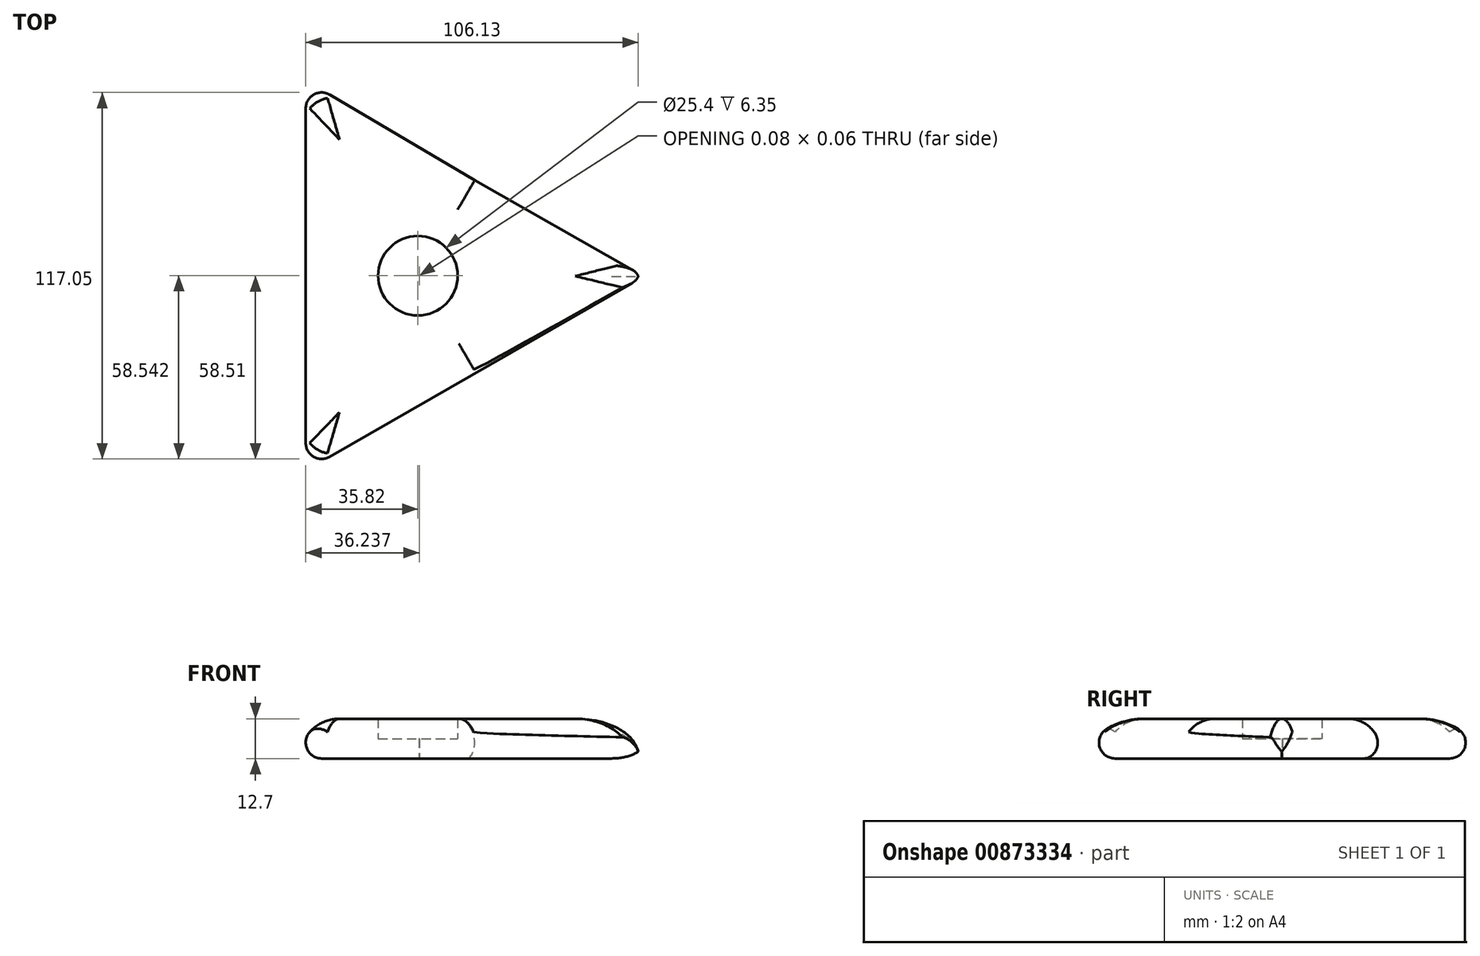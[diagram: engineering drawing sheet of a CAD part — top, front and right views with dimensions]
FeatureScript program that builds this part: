
annotation { "Feature Type Name" : "Feature", "Feature Type Description" : "" }
export const myFeature = defineFeature(function(context is Context, id is Id, definition is map)
    precondition{}
    {
        {
            var Q0;
            Q0=qCreatedBy(makeId("Top.planeOp"),FACE);
            var sketch = newSketch(context, id + "F0", { "sketchPlane" : qUnion([Q0])});
            skCircle(sketch, "E0", {"center": v(0, 0) * mm, "radius": 12.7 * mm});
            skSolve(sketch);
        }
        {
            var Q0;
            Q0=qCreatedBy(makeId("Top.planeOp"),FACE);
            var sketch = newSketch(context, id + "F1", { "sketchPlane" : qUnion([Q0])});
            skLineSegment(sketch, "E1", {"start": v(-37.76, 65.76) * mm, "end": v(19.45, -32.69) * mm});
            skLineSegment(sketch, "E2", {"start": v(19.45, -32.69) * mm, "end": v(75.7, 0) * mm});
            skLineSegment(sketch, "E3", {"start": v(75.7, 0) * mm, "end": v(-37.76, 0) * mm});
            skLineSegment(sketch, "E4", {"start": v(-37.76, 0) * mm, "end": v(-37.76, -65.56) * mm});
            skLineSegment(sketch, "E5", {"start": v(-37.76, -65.56) * mm, "end": v(19.09, 32.16) * mm});
            skLineSegment(sketch, "E6", {"start": v(19.09, 32.16) * mm, "end": v(-37.76, 65.76) * mm});
            skLineSegment(sketch, "E7", {"start": v(-37.76, 65.76) * mm, "end": v(-37.76, 0) * mm});
            skLineSegment(sketch, "E8", {"start": v(-37.76, 0) * mm, "end": v(75.7, 0) * mm});
            skLineSegment(sketch, "E9", {"start": v(19.09, 32.16) * mm, "end": v(75.7, 0) * mm});
            skLineSegment(sketch, "E10", {"start": v(-37.76, -65.56) * mm, "end": v(19.45, -32.69) * mm});
            skSolve(sketch);
        }
        {
            var Q0;
            Q0 = qSketchRegion(id + "F1", true);
            extrude(context, id + "F2", {"entities" : qUnion([Q0]), "endBound" : BoundingType.SYMMETRIC, "depth" : 12.7 * mm, "offsetDistance" : 25.4 * mm});
        }
        {
            var Q0;
            Q0=makeQuery(id+"F2.opExtrude","CAP_EDGE",EDGE,{"disambiguationData":[OSD([sQuery(id+"F1.wireOp",EDGE,"E4"),sQuery(id+"F1.wireOp",EDGE,"E7")])],"isStart":false});
            var Q1;
            Q1=makeQuery(id+"F2.opExtrude","CAP_EDGE",EDGE,{"disambiguationData":[OSD([sQuery(id+"F1.wireOp",EDGE,"E9")])],"isStart":false});
            var Q2;
            Q2=makeQuery(id+"F2.opExtrude","CAP_EDGE",EDGE,{"disambiguationData":[OSD([sQuery(id+"F1.wireOp",EDGE,"E6")])],"isStart":false});
            var Q3;
            Q3=makeQuery(id+"F2.opExtrude","CAP_EDGE",EDGE,{"disambiguationData":[OSD([sQuery(id+"F1.wireOp",EDGE,"E10")])],"isStart":false});
            fillet(context, id + "F3", {"entities" : qUnion([Q0, Q1, Q2, Q3]), "radius" : 12.7 * mm, "tangentPropagation" : true, "allowEdgeOverflow" : false});
        }
        {
            var Q0;
            {var subQ0=sQuery(id+"F1.wireOp",EDGE,"E7");var subQ1=sQuery(id+"F1.wireOp",EDGE,"E4");Q0=makeQuery(id+"F3.opFillet","BLEND_EDGE",EDGE,{"blendedFrom":[makeQuery(id+"F2.opExtrude","CAP_EDGE",EDGE,{"disambiguationData":[OSD([subQ1,subQ0])],"isStart":false}),makeQuery(id+"F2.opExtrude","CAP_FACE",FACE,{"disambiguationData":[OSD([sQuery(id+"F1.wireOp",EDGE,"E1"),sQuery(id+"F1.wireOp",EDGE,"E2"),subQ1,sQuery(id+"F1.wireOp",EDGE,"E5"),sQuery(id+"F1.wireOp",EDGE,"E6"),subQ0,sQuery(id+"F1.wireOp",EDGE,"E8"),sQuery(id+"F1.wireOp",EDGE,"E9"),sQuery(id+"F1.wireOp",EDGE,"E10")])],"isStart":true})],"blendedInto":[makeQuery(id+"F2.opExtrude","CAP_FACE",FACE,{"disambiguationData":[OSD([sQuery(id+"F1.wireOp",EDGE,"E1"),sQuery(id+"F1.wireOp",EDGE,"E2"),subQ1,sQuery(id+"F1.wireOp",EDGE,"E5"),sQuery(id+"F1.wireOp",EDGE,"E6"),subQ0,sQuery(id+"F1.wireOp",EDGE,"E8"),sQuery(id+"F1.wireOp",EDGE,"E9"),sQuery(id+"F1.wireOp",EDGE,"E10")])],"isStart":true})]});}
            var Q1;
            {var subQ0=sQuery(id+"F1.wireOp",EDGE,"E10");Q1=makeQuery(id+"F3.opFillet","BLEND_EDGE",EDGE,{"disambiguationData":[OD(0.0)],"blendedFrom":[makeQuery(id+"F2.opExtrude","CAP_EDGE",EDGE,{"disambiguationData":[OSD([subQ0])],"isStart":false}),makeQuery(id+"F2.opExtrude","CAP_FACE",FACE,{"disambiguationData":[OSD([sQuery(id+"F1.wireOp",EDGE,"E1"),sQuery(id+"F1.wireOp",EDGE,"E2"),sQuery(id+"F1.wireOp",EDGE,"E4"),sQuery(id+"F1.wireOp",EDGE,"E5"),sQuery(id+"F1.wireOp",EDGE,"E6"),sQuery(id+"F1.wireOp",EDGE,"E7"),sQuery(id+"F1.wireOp",EDGE,"E8"),sQuery(id+"F1.wireOp",EDGE,"E9"),subQ0])],"isStart":true})],"blendedInto":[makeQuery(id+"F2.opExtrude","CAP_FACE",FACE,{"disambiguationData":[OSD([sQuery(id+"F1.wireOp",EDGE,"E1"),sQuery(id+"F1.wireOp",EDGE,"E2"),sQuery(id+"F1.wireOp",EDGE,"E4"),sQuery(id+"F1.wireOp",EDGE,"E5"),sQuery(id+"F1.wireOp",EDGE,"E6"),sQuery(id+"F1.wireOp",EDGE,"E7"),sQuery(id+"F1.wireOp",EDGE,"E8"),sQuery(id+"F1.wireOp",EDGE,"E9"),subQ0])],"isStart":true})]});}
            var Q2;
            {var subQ0=sQuery(id+"F1.wireOp",EDGE,"E9");Q2=makeQuery(id+"F3.opFillet","BLEND_EDGE",EDGE,{"blendedFrom":[makeQuery(id+"F2.opExtrude","CAP_EDGE",EDGE,{"disambiguationData":[OSD([subQ0])],"isStart":false}),makeQuery(id+"F2.opExtrude","CAP_FACE",FACE,{"disambiguationData":[OSD([sQuery(id+"F1.wireOp",EDGE,"E1"),sQuery(id+"F1.wireOp",EDGE,"E2"),sQuery(id+"F1.wireOp",EDGE,"E4"),sQuery(id+"F1.wireOp",EDGE,"E5"),sQuery(id+"F1.wireOp",EDGE,"E6"),sQuery(id+"F1.wireOp",EDGE,"E7"),sQuery(id+"F1.wireOp",EDGE,"E8"),subQ0,sQuery(id+"F1.wireOp",EDGE,"E10")])],"isStart":true})],"blendedInto":[makeQuery(id+"F2.opExtrude","CAP_FACE",FACE,{"disambiguationData":[OSD([sQuery(id+"F1.wireOp",EDGE,"E1"),sQuery(id+"F1.wireOp",EDGE,"E2"),sQuery(id+"F1.wireOp",EDGE,"E4"),sQuery(id+"F1.wireOp",EDGE,"E5"),sQuery(id+"F1.wireOp",EDGE,"E6"),sQuery(id+"F1.wireOp",EDGE,"E7"),sQuery(id+"F1.wireOp",EDGE,"E8"),subQ0,sQuery(id+"F1.wireOp",EDGE,"E10")])],"isStart":true})]});}
            var Q3;
            Q3=makeQuery(id+"F3.opFillet","BLEND_EDGE",EDGE,{"blendedFrom":[makeQuery(id+"F2.opExtrude","CAP_EDGE",EDGE,{"disambiguationData":[OSD([sQuery(id+"F1.wireOp",EDGE,"E9")])],"isStart":false}),makeQuery(id+"F2.opExtrude","CAP_EDGE",EDGE,{"disambiguationData":[OSD([sQuery(id+"F1.wireOp",EDGE,"E10")])],"isStart":false})],"blendedInto":[]});
            var Q4;
            Q4=makeQuery(id+"F3.opFillet","BLEND_EDGE",EDGE,{"blendedFrom":[makeQuery(id+"F2.opExtrude","CAP_EDGE",EDGE,{"disambiguationData":[OSD([sQuery(id+"F1.wireOp",EDGE,"E4"),sQuery(id+"F1.wireOp",EDGE,"E7")])],"isStart":false}),makeQuery(id+"F2.opExtrude","CAP_EDGE",EDGE,{"disambiguationData":[OSD([sQuery(id+"F1.wireOp",EDGE,"E6")])],"isStart":false})],"blendedInto":[]});
            var Q5;
            Q5=makeQuery(id+"F3.opFillet","BLEND_EDGE",EDGE,{"blendedFrom":[makeQuery(id+"F2.opExtrude","CAP_EDGE",EDGE,{"disambiguationData":[OSD([sQuery(id+"F1.wireOp",EDGE,"E4"),sQuery(id+"F1.wireOp",EDGE,"E7")])],"isStart":false}),makeQuery(id+"F2.opExtrude","CAP_EDGE",EDGE,{"disambiguationData":[OSD([sQuery(id+"F1.wireOp",EDGE,"E10")])],"isStart":false})],"blendedInto":[]});
            fillet(context, id + "F4", {"entities" : qUnion([Q0, Q1, Q2, Q3, Q4, Q5]), "radius" : 5.08 * mm, "tangentPropagation" : true, "allowEdgeOverflow" : false});
        }
        {
            var Q0;
            Q0=sQuery(id+"F0.wireOp",VERTEX,"E0.center");
            var Q1;
            Q1=makeQuery(id+"F2.opExtrude","SWEPT_BODY",BODY,{"disambiguationData":[OSD([sQuery(id+"F1.wireOp",EDGE,"E1"),sQuery(id+"F1.wireOp",EDGE,"E2"),sQuery(id+"F1.wireOp",EDGE,"E4"),sQuery(id+"F1.wireOp",EDGE,"E5"),sQuery(id+"F1.wireOp",EDGE,"E6"),sQuery(id+"F1.wireOp",EDGE,"E7"),sQuery(id+"F1.wireOp",EDGE,"E8"),sQuery(id+"F1.wireOp",EDGE,"E9"),sQuery(id+"F1.wireOp",EDGE,"E10")])]});
            hole(context, id + "F5", {"style" : HoleStyle.SIMPLE, "endStyle" : HoleEndStyle.THROUGH, "oppositeDirection" : true, "holeDiameter" : 25.4 * mm, "majorDiameter" : 6.35 * mm, "isTappedThrough" : true, "tappedDepth" : 12.7 * mm, "tapClearance" : 3, "locations" : qUnion([Q0]), "scope" : qUnion([Q1])});
        }
    });
